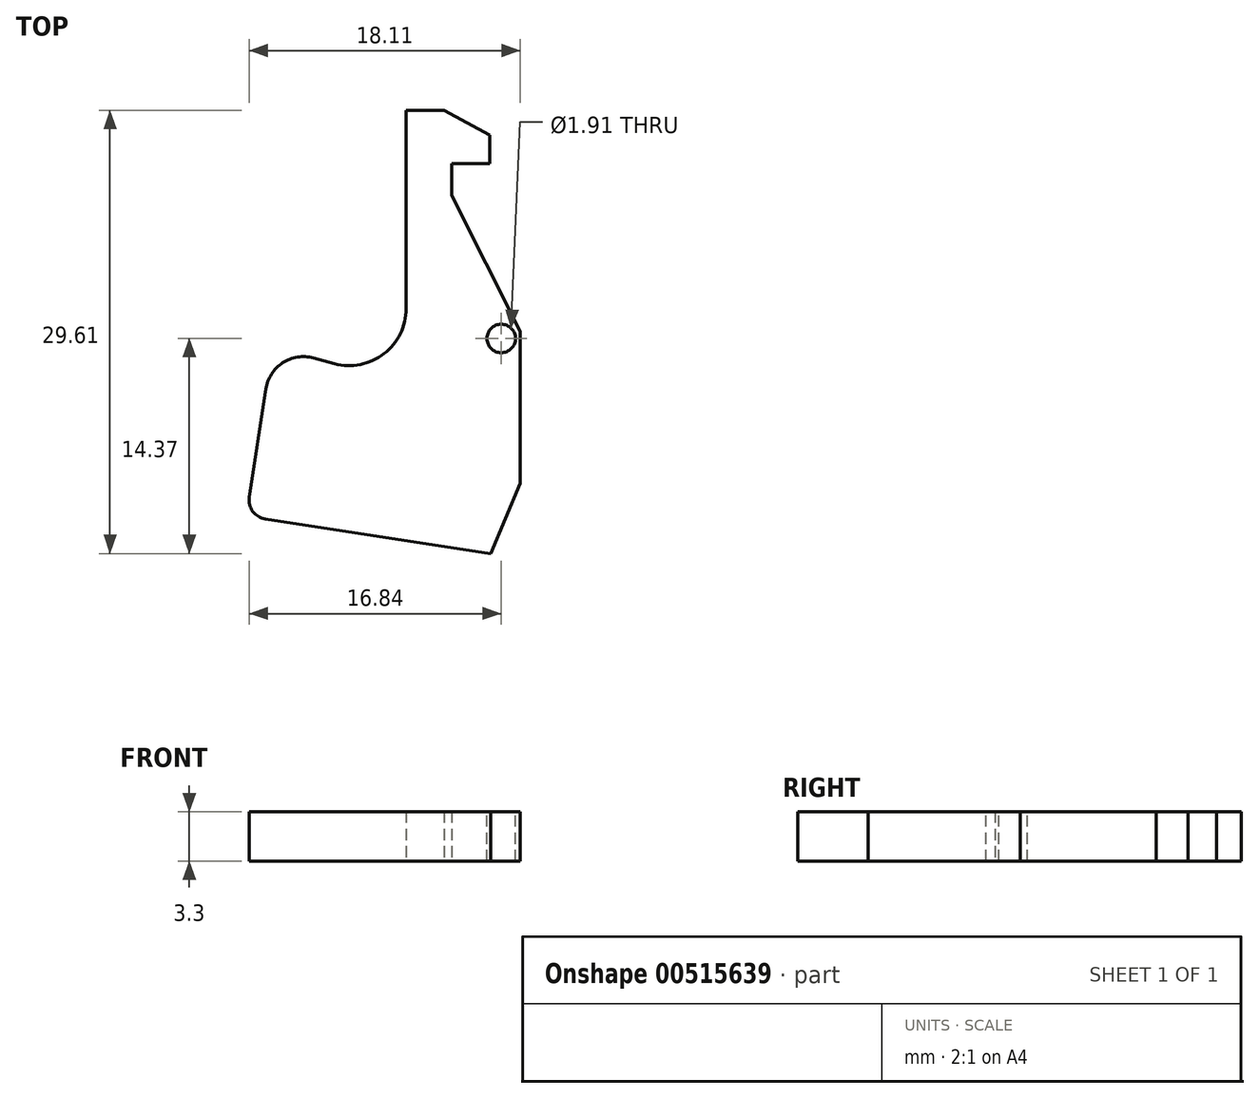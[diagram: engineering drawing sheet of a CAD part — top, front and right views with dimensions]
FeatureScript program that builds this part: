
annotation { "Feature Type Name" : "Feature", "Feature Type Description" : "" }
export const myFeature = defineFeature(function(context is Context, id is Id, definition is map)
    precondition{}
    {
        {
            var Q0;
            Q0=qCreatedBy(makeId("Top.planeOp"),FACE);
            var sketch = newSketch(context, id + "F0", { "sketchPlane" : qUnion([Q0])});
            skLineSegment(sketch, "E0", {"start": v(0, 0) * mm, "end": v(0, -18.2) * mm});
            skLineSegment(sketch, "E1", {"start": v(0, -18.2) * mm, "end": v(-8.94, -15.81) * mm});
            skLineSegment(sketch, "E2", {"start": v(-8.94, -15.81) * mm, "end": v(-10.67, -27.11) * mm});
            skLineSegment(sketch, "E3", {"start": v(-10.67, -27.11) * mm, "end": v(5.65, -29.6) * mm});
            skLineSegment(sketch, "E4", {"start": v(7.62, -24.93) * mm, "end": v(7.62, -14.77) * mm});
            skLineSegment(sketch, "E5", {"start": v(7.62, -14.77) * mm, "end": v(3.05, -5.7) * mm});
            skLineSegment(sketch, "E6", {"start": v(3.05, -5.7) * mm, "end": v(3.05, -3.55) * mm});
            skLineSegment(sketch, "E7", {"start": v(3.05, -3.55) * mm, "end": v(5.59, -3.55) * mm});
            skLineSegment(sketch, "E8", {"start": v(5.59, -3.55) * mm, "end": v(5.59, -1.64) * mm});
            skLineSegment(sketch, "E9", {"start": v(5.59, -1.64) * mm, "end": v(2.54, 0) * mm});
            skLineSegment(sketch, "E10", {"start": v(2.54, 0) * mm, "end": v(0, 0) * mm});
            skLineSegment(sketch, "E11", {"start": v(7.62, -24.93) * mm, "end": v(5.65, -29.6) * mm});
            skSolve(sketch);
        }
        {
            var Q0;
            Q0 = qSketchRegion(id + "F0", true);
            extrude(context, id + "F1", {"entities" : qUnion([Q0]), "depth" : 3.3 * mm, "offsetDistance" : 25.4 * mm});
        }
        {
            var Q0;
            Q0=makeQuery(id+"F1.opExtrude","SWEPT_EDGE",EDGE,{"disambiguationData":[OSD([sQuery(id+"F0.wireOp",EDGE,"E0"),sQuery(id+"F0.wireOp",EDGE,"E1")])]});
            fillet(context, id + "F2", {"entities" : qUnion([Q0]), "radius" : 3.8 * mm, "tangentPropagation" : true, "allowEdgeOverflow" : false});
        }
        {
            var Q0;
            Q0=makeQuery(id+"F1.opExtrude","SWEPT_EDGE",EDGE,{"disambiguationData":[OSD([sQuery(id+"F0.wireOp",EDGE,"E1"),sQuery(id+"F0.wireOp",EDGE,"E2")])]});
            fillet(context, id + "F3", {"entities" : qUnion([Q0]), "radius" : 2.54 * mm, "tangentPropagation" : true, "allowEdgeOverflow" : false});
        }
        {
            var Q0;
            Q0=makeQuery(id+"F1.opExtrude","CAP_FACE",FACE,{"disambiguationData":[OSD([sQuery(id+"F0.wireOp",EDGE,"E0"),sQuery(id+"F0.wireOp",EDGE,"E1"),sQuery(id+"F0.wireOp",EDGE,"E2"),sQuery(id+"F0.wireOp",EDGE,"E3"),sQuery(id+"F0.wireOp",EDGE,"E4"),sQuery(id+"F0.wireOp",EDGE,"E5"),sQuery(id+"F0.wireOp",EDGE,"E6"),sQuery(id+"F0.wireOp",EDGE,"E7"),sQuery(id+"F0.wireOp",EDGE,"E8"),sQuery(id+"F0.wireOp",EDGE,"E9"),sQuery(id+"F0.wireOp",EDGE,"E10"),sQuery(id+"F0.wireOp",EDGE,"E11")])],"isStart":false});
            var sketch = newSketch(context, id + "F4", { "sketchPlane" : qUnion([Q0])});
            skPoint(sketch, "E12", {"position": v(6.35, -15.24) * mm});
            skSolve(sketch);
        }
        {
            var Q0;
            Q0=sQuery(id+"F4.wireOp",VERTEX,"E12");
            var Q1;
            Q1=makeQuery(id+"F1.opExtrude","SWEPT_BODY",BODY,{"disambiguationData":[OSD([sQuery(id+"F0.wireOp",EDGE,"E0"),sQuery(id+"F0.wireOp",EDGE,"E1"),sQuery(id+"F0.wireOp",EDGE,"E2"),sQuery(id+"F0.wireOp",EDGE,"E3"),sQuery(id+"F0.wireOp",EDGE,"E4"),sQuery(id+"F0.wireOp",EDGE,"E5"),sQuery(id+"F0.wireOp",EDGE,"E6"),sQuery(id+"F0.wireOp",EDGE,"E7"),sQuery(id+"F0.wireOp",EDGE,"E8"),sQuery(id+"F0.wireOp",EDGE,"E9"),sQuery(id+"F0.wireOp",EDGE,"E10"),sQuery(id+"F0.wireOp",EDGE,"E11")])]});
            hole(context, id + "F5", {"style" : HoleStyle.SIMPLE, "endStyle" : HoleEndStyle.THROUGH, "holeDiameter" : 1.9 * mm, "isTappedThrough" : true, "tappedDepth" : 12.7 * mm, "tapClearance" : 3, "locations" : qUnion([Q0]), "scope" : qUnion([Q1])});
        }
        {
            var Q0;
            Q0=makeQuery(id+"F1.opExtrude","SWEPT_EDGE",EDGE,{"disambiguationData":[OSD([sQuery(id+"F0.wireOp",EDGE,"E2"),sQuery(id+"F0.wireOp",EDGE,"E3")])]});
            fillet(context, id + "F6", {"entities" : qUnion([Q0]), "radius" : 1.27 * mm, "tangentPropagation" : true, "allowEdgeOverflow" : false});
        }
    });
